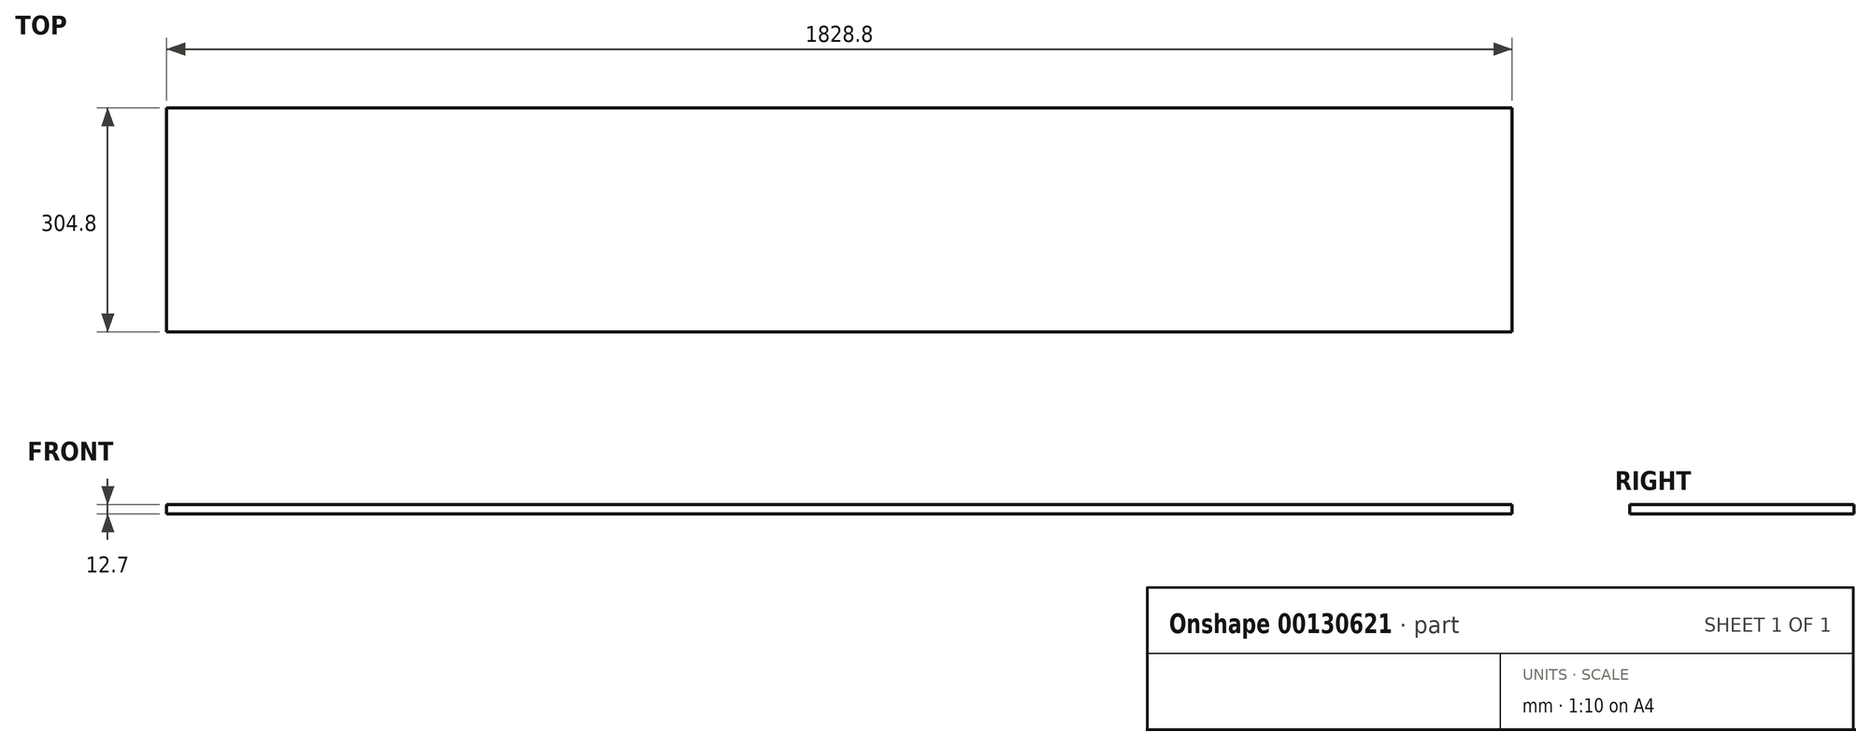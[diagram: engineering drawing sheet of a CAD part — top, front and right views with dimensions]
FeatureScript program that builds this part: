
annotation { "Feature Type Name" : "Feature", "Feature Type Description" : "" }
export const myFeature = defineFeature(function(context is Context, id is Id, definition is map)
    precondition{}
    {
        {
            var Q0;
            Q0=qCreatedBy(makeId("Top.planeOp"),FACE);
            var sketch = newSketch(context, id + "F0", { "sketchPlane" : qUnion([Q0])});
            skLineSegment(sketch, "E0.bottom", {"start": v(-307.42, 156) * mm, "end": v(1521.38, 156) * mm});
            skLineSegment(sketch, "E0.top", {"start": v(-307.42, -148.8) * mm, "end": v(1521.38, -148.8) * mm});
            skLineSegment(sketch, "E0.left", {"start": v(-307.42, 156) * mm, "end": v(-307.42, -148.8) * mm});
            skLineSegment(sketch, "E0.right", {"start": v(1521.38, 156) * mm, "end": v(1521.38, -148.8) * mm});
            skSolve(sketch);
        }
        {
            var Q0;
            Q0=makeQuery(id+"F0.imprint","IMPRINT",FACE,{"disambiguationData":[TD([[makeQuery(id+"F0.imprint","IMPRINT",EDGE,{"derivedFrom":sQuery(id+"F0.wireOp",EDGE,"E0.bottom")}),-1.0]])]});
            extrude(context, id + "F1", {"entities" : qUnion([Q0]), "depth" : 12.7 * mm});
        }
    });
